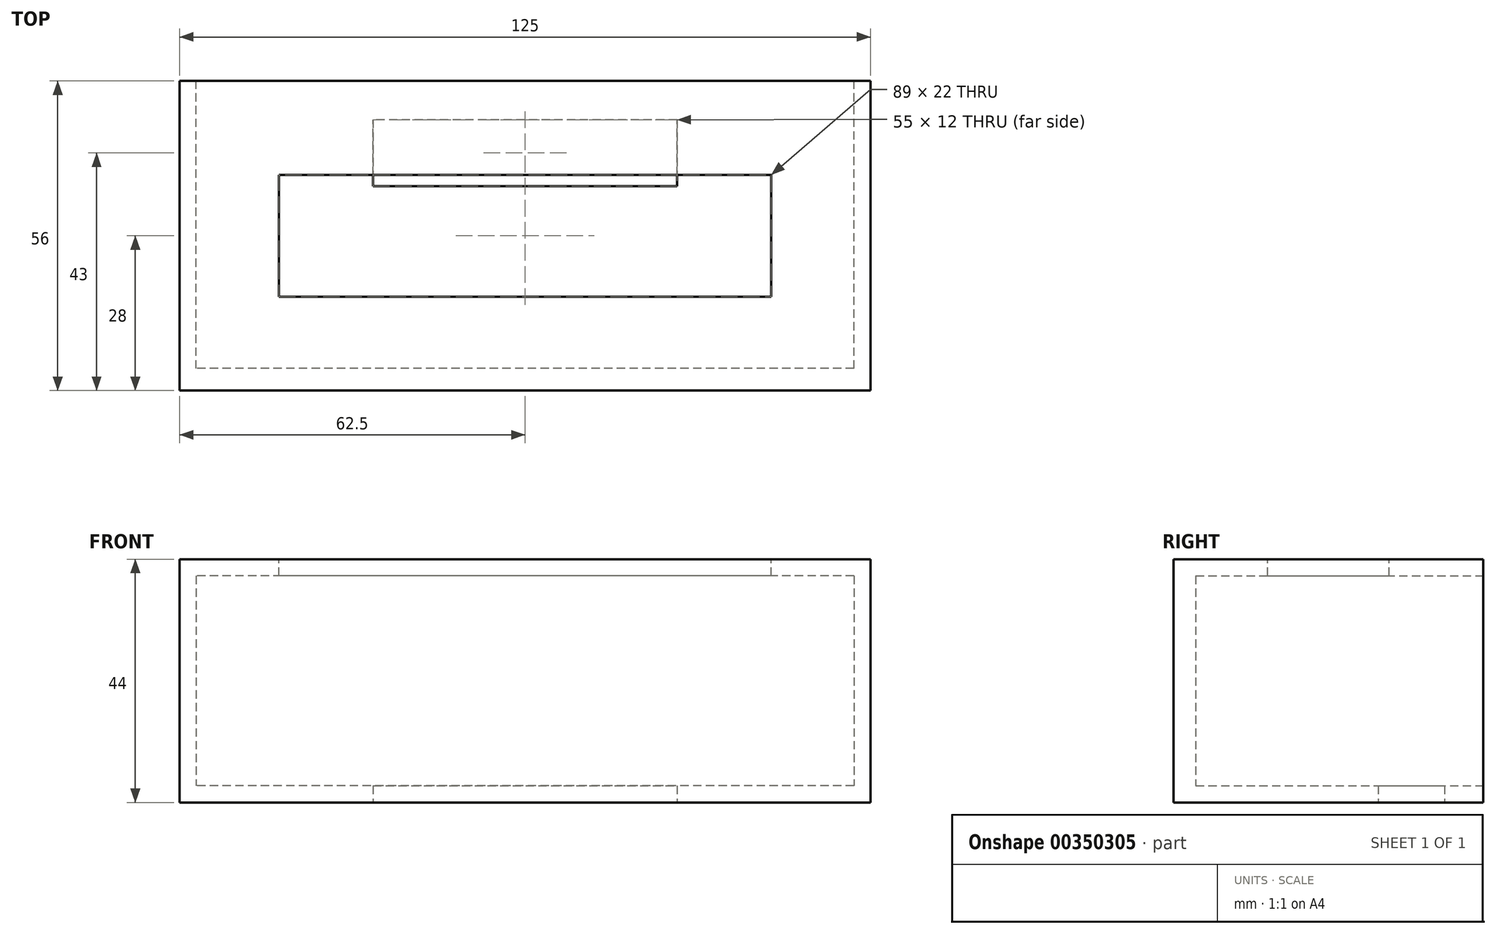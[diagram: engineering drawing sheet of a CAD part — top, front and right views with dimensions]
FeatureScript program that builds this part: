
annotation { "Feature Type Name" : "Feature", "Feature Type Description" : "" }
export const myFeature = defineFeature(function(context is Context, id is Id, definition is map)
    precondition{}
    {
        {
            var Q0;
            Q0=qCreatedBy(makeId("Top.planeOp"),FACE);
            var sketch = newSketch(context, id + "F0", { "sketchPlane" : qUnion([Q0])});
            skLineSegment(sketch, "E0.bottom", {"start": v(62.5, -28) * mm, "end": v(-62.5, -28) * mm});
            skLineSegment(sketch, "E0.top", {"start": v(62.5, 28) * mm, "end": v(-62.5, 28) * mm});
            skLineSegment(sketch, "E0.left", {"start": v(62.5, -28) * mm, "end": v(62.5, 28) * mm});
            skLineSegment(sketch, "E0.right", {"start": v(-62.5, -28) * mm, "end": v(-62.5, 28) * mm});
            skPoint(sketch, "E0.middle", {"position": v(0, 0) * mm});
            skSolve(sketch);
        }
        {
            var Q0;
            Q0 = qSketchRegion(id + "F0", true);
            extrude(context, id + "F1", {"entities" : qUnion([Q0]), "oppositeDirection" : true, "depth" : 44 * mm});
        }
        {
            var Q0;
            Q0=makeQuery(id+"F1.opExtrude","CAP_FACE",FACE,{"disambiguationData":[OSD([sQuery(id+"F0.wireOp",EDGE,"E0.bottom"),sQuery(id+"F0.wireOp",EDGE,"E0.top"),sQuery(id+"F0.wireOp",EDGE,"E0.left"),sQuery(id+"F0.wireOp",EDGE,"E0.right")])],"isStart":true});
            var sketch = newSketch(context, id + "F2", { "sketchPlane" : qUnion([Q0])});
            skLineSegment(sketch, "E1.bottom", {"start": v(44.5, -11) * mm, "end": v(-44.5, -11) * mm});
            skLineSegment(sketch, "E1.top", {"start": v(44.5, 11) * mm, "end": v(-44.5, 11) * mm});
            skLineSegment(sketch, "E1.left", {"start": v(44.5, -11) * mm, "end": v(44.5, 11) * mm});
            skLineSegment(sketch, "E1.right", {"start": v(-44.5, -11) * mm, "end": v(-44.5, 11) * mm});
            skPoint(sketch, "E1.middle", {"position": v(0, 0) * mm});
            skSolve(sketch);
        }
        {
            var Q0;
            Q0=makeQuery(id+"F1.opExtrude","CAP_FACE",FACE,{"disambiguationData":[OSD([sQuery(id+"F0.wireOp",EDGE,"E0.bottom"),sQuery(id+"F0.wireOp",EDGE,"E0.top"),sQuery(id+"F0.wireOp",EDGE,"E0.left"),sQuery(id+"F0.wireOp",EDGE,"E0.right")])],"isStart":false});
            var sketch = newSketch(context, id + "F3", { "sketchPlane" : qUnion([Q0])});
            skLineSegment(sketch, "E2.bottom", {"start": v(27.5, -21) * mm, "end": v(-27.5, -21) * mm});
            skLineSegment(sketch, "E2.top", {"start": v(27.5, -9) * mm, "end": v(-27.5, -9) * mm});
            skLineSegment(sketch, "E2.left", {"start": v(27.5, -21) * mm, "end": v(27.5, -9) * mm});
            skLineSegment(sketch, "E2.right", {"start": v(-27.5, -21) * mm, "end": v(-27.5, -9) * mm});
            skPoint(sketch, "E2.middle", {"position": v(0, -15) * mm});
            skSolve(sketch);
        }
        {
            var Q0;
            Q0 = qSketchRegion(id + "F3", true);
            extrude(context, id + "F4", {"entities" : qUnion([Q0]), "operationType" : NewBodyOperationType.REMOVE, "oppositeDirection" : true, "depth" : 13 * mm});
        }
        {
            var Q0;
            Q0 = qSketchRegion(id + "F2", true);
            extrude(context, id + "F5", {"entities" : qUnion([Q0]), "operationType" : NewBodyOperationType.REMOVE, "oppositeDirection" : true, "depth" : 17 * mm});
        }
        {
            var Q0;
            Q0=makeQuery(id+"F1.opExtrude","SWEPT_FACE",FACE,{"disambiguationData":[OSD([sQuery(id+"F0.wireOp",EDGE,"E0.top")])]});
            var sketch = newSketch(context, id + "F6", { "sketchPlane" : qUnion([Q0])});
            skLineSegment(sketch, "E3.bottom", {"start": v(-59.5, -3) * mm, "end": v(59.5, -3) * mm});
            skLineSegment(sketch, "E3.top", {"start": v(-59.5, -41) * mm, "end": v(59.5, -41) * mm});
            skLineSegment(sketch, "E3.left", {"start": v(-59.5, -3) * mm, "end": v(-59.5, -41) * mm});
            skLineSegment(sketch, "E3.right", {"start": v(59.5, -3) * mm, "end": v(59.5, -41) * mm});
            skPoint(sketch, "E3.middle", {"position": v(0, -22) * mm});
            skPoint(sketch, "E3.middle.positionSnap0", {"position": v(62.5, -22) * mm});
            skPoint(sketch, "E3.middle.positionSnap1", {"position": v(0, -44) * mm});
            skPoint(sketch, "E3.centerSnap0", {"position": v(62.5, -22) * mm});
            skPoint(sketch, "E3.centerSnap1", {"position": v(0, -44) * mm});
            skSolve(sketch);
        }
        {
            var Q0;
            Q0 = qSketchRegion(id + "F6", true);
            extrude(context, id + "F7", {"entities" : qUnion([Q0]), "operationType" : NewBodyOperationType.REMOVE, "oppositeDirection" : true, "depth" : 52 * mm});
        }
    });
